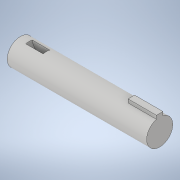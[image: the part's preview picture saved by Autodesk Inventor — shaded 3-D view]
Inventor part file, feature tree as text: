
AUTODESK INVENTOR PART (.ipt)
format: ipt  version: 2021 (Build 250183000, 183)  size: 114,688 bytes
history: native  units: in
note: dims shown in document units (in); Inventor stores cm internally (conversion verified against a paired STEP export)
features: extrude x3, sketch x3
ambient origin geometry x8: Origin, YZ Plane, XZ Plane, XY Plane, X Axis, Y Axis, Z Axis, Center Point
bodies: Solid1 (feature_tree)
feature tree (6):
  extrude  "Extrusion1"  Depth=4.0in TaperAngle=0.0deg
  extrude  "Extrusion2"  Depth=0.188in
  extrude  "Extrusion3"  Depth=0.188in
  sketch  "Sketch1"  dims[d0=0.75in d1=4.0in d2=0.0in]
  sketch  "Sketch2"  dims[d3=0.1in d4=0.188in]
  sketch  "Sketch3"  dims[d5=0.813in d6=0.0in d7=0.5in d8=0.5in d9=0.188in d10=0.0in]
